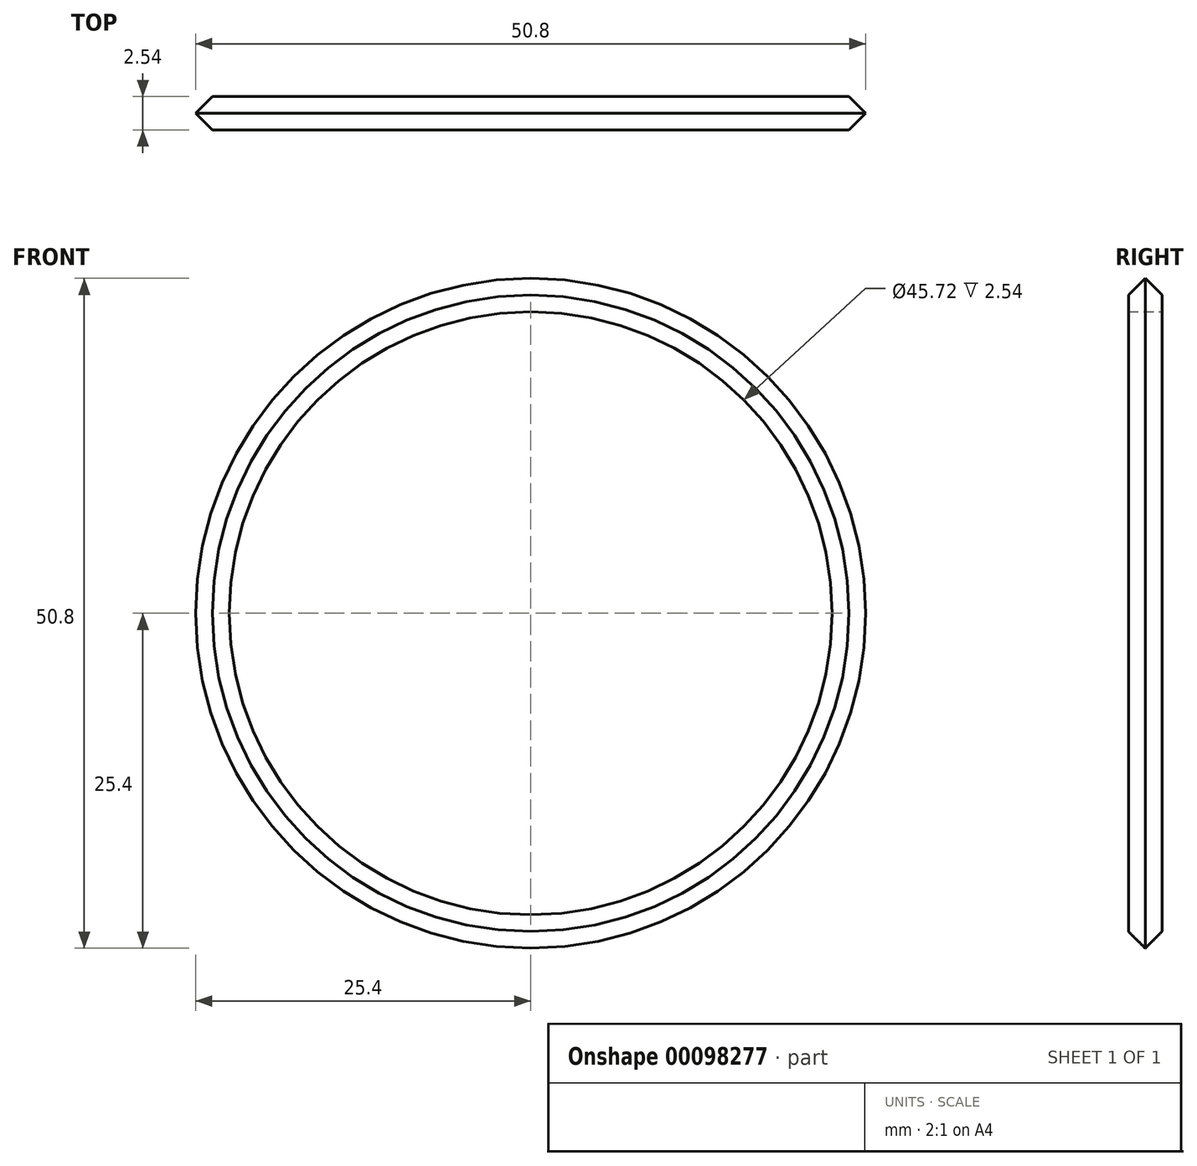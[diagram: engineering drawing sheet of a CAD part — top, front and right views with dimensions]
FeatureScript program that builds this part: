
annotation { "Feature Type Name" : "Feature", "Feature Type Description" : "" }
export const myFeature = defineFeature(function(context is Context, id is Id, definition is map)
    precondition{}
    {
        {
            var Q0;
            Q0=qCreatedBy(makeId("Front.planeOp"),FACE);
            var sketch = newSketch(context, id + "F0", { "sketchPlane" : qUnion([Q0])});
            skCircle(sketch, "E0", {"center": v(0, 0) * mm, "radius": 25.4 * mm});
            skSolve(sketch);
        }
        {
            var Q0;
            Q0=makeQuery(id+"F0.imprint","IMPRINT",FACE,{"disambiguationData":[TD([[makeQuery(id+"F0.imprint","IMPRINT",EDGE,{"derivedFrom":sQuery(id+"F0.wireOp",EDGE,"E0")}),1.0]])]});
            extrude(context, id + "F1", {"entities" : qUnion([Q0]), "depth" : 2.54 * mm});
        }
        {
            var Q0;
            Q0=sQuery(id+"F0.wireOp",VERTEX,"E0.center");
            var Q1;
            Q1=makeQuery(id+"F1.opExtrude","SWEPT_BODY",BODY,{"disambiguationData":[OSD([sQuery(id+"F0.wireOp",EDGE,"E0")])]});
            hole(context, id + "F2", {"style" : HoleStyle.SIMPLE, "endStyle" : HoleEndStyle.THROUGH, "oppositeDirection" : true, "holeDiameter" : 45.72 * mm, "locations" : qUnion([Q0]), "scope" : qUnion([Q1]), "isTappedThrough" : true});
        }
        {
            var Q0;
            Q0=makeQuery(id+"F2.hole-0.boolean.opBoolean","INTERSECT",EDGE,{"derivedFrom":[makeQuery(id+"F1.opExtrude","CAP_FACE",FACE,{"disambiguationData":[OSD([sQuery(id+"F0.wireOp",EDGE,"E0")])],"isStart":false}),makeQuery(id+"F2.hole-0.opRevolve","SWEPT_FACE",FACE,{"disambiguationData":[OSD([sQuery(id+"F2.hole-0.sketch.wireOp",EDGE,"core_line_2")])]})]});
            var Q1;
            Q1=makeQuery(id+"F1.opExtrude","CAP_EDGE",EDGE,{"disambiguationData":[OSD([sQuery(id+"F0.wireOp",EDGE,"E0")])],"isStart":false});
            var Q2;
            Q2=makeQuery(id+"F1.opExtrude","CAP_EDGE",EDGE,{"disambiguationData":[OSD([sQuery(id+"F0.wireOp",EDGE,"E0")])],"isStart":true});
            var Q3;
            Q3=makeQuery(id+"F2.hole-0.boolean.opBoolean","COPY",EDGE,{"derivedFrom":makeQuery(id+"F2.hole-0.opRevolve","SWEPT_EDGE",EDGE,{"disambiguationData":[OSD([sQuery(id+"F2.hole-0.sketch.wireOp",EDGE,"core_line_2"),sQuery(id+"F2.hole-0.sketch.wireOp",EDGE,"core_line_3")])]})});
            chamfer(context, id + "F3", {"entities" : qUnion([Q0, Q1, Q2, Q3]), "width" : 1.27 * mm, "tangentPropagation" : true});
        }
    });
